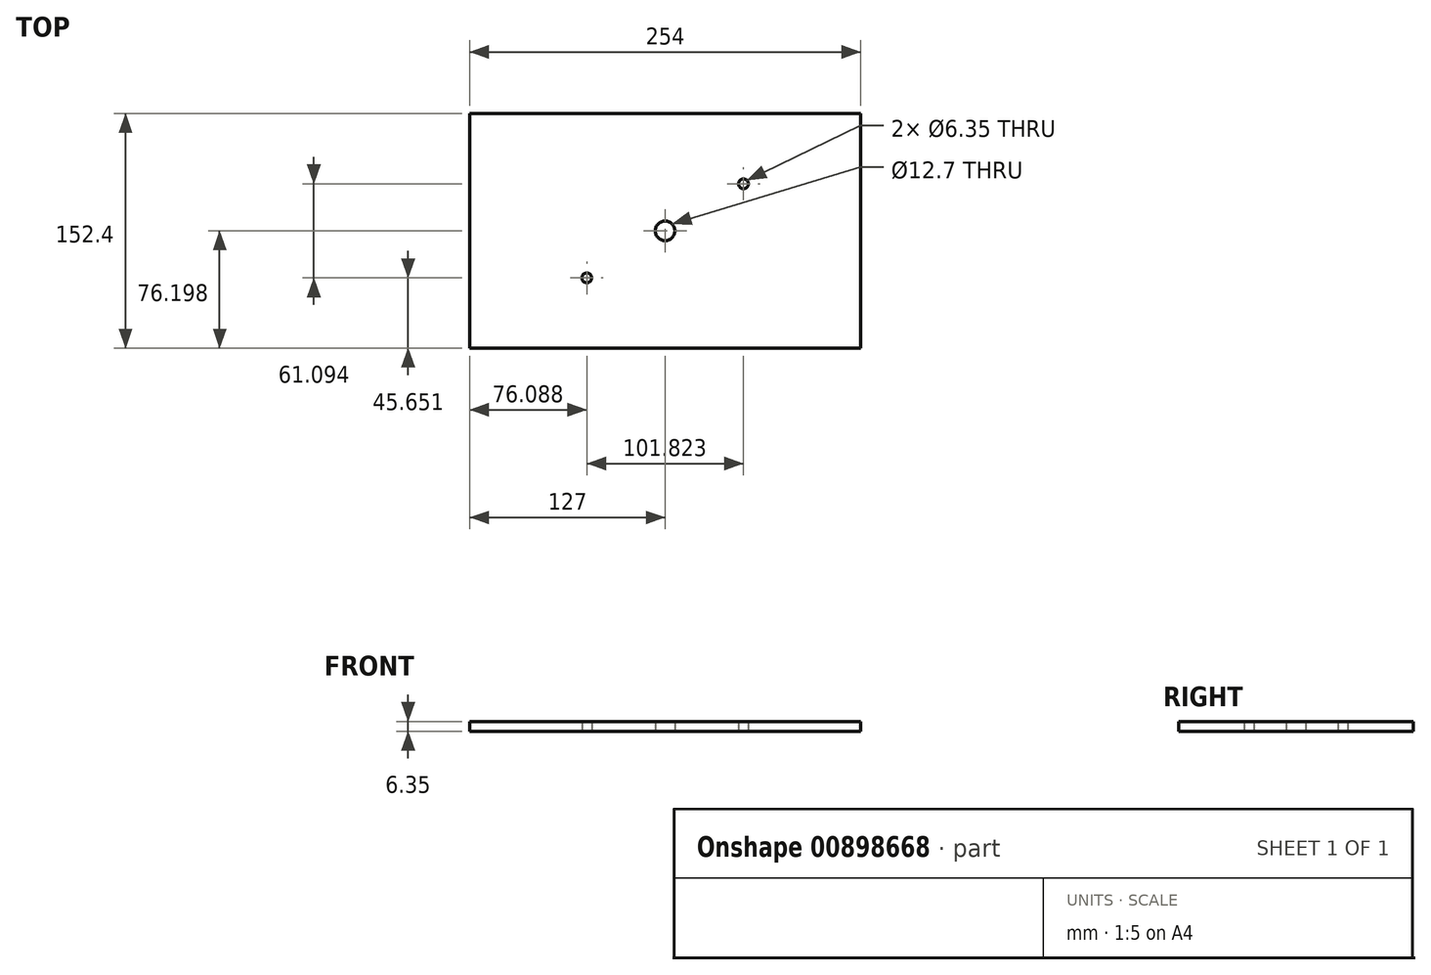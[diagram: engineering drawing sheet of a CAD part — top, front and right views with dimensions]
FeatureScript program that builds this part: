
annotation { "Feature Type Name" : "Feature", "Feature Type Description" : "" }
export const myFeature = defineFeature(function(context is Context, id is Id, definition is map)
    precondition{}
    {
        {
            var Q0;
            Q0=qCreatedBy(makeId("Top.planeOp"),FACE);
            var sketch = newSketch(context, id + "F0", { "sketchPlane" : qUnion([Q0])});
            skLineSegment(sketch, "E0", {"start": v(-26.31, -26.64) * mm, "end": v(227.69, -26.64) * mm});
            skLineSegment(sketch, "E1", {"start": v(227.69, -26.64) * mm, "end": v(227.69, 125.76) * mm});
            skLineSegment(sketch, "E2", {"start": v(227.69, 125.76) * mm, "end": v(-26.31, 125.76) * mm});
            skLineSegment(sketch, "E3", {"start": v(-26.31, 125.76) * mm, "end": v(-26.31, -26.64) * mm});
            skLineSegment(sketch, "E4", {"start": v(100.69, 125.76) * mm, "end": v(100.69, -26.64) * mm, "construction": true});
            skCircle(sketch, "E5", {"center": v(100.69, 49.56) * mm, "radius": 6.35 * mm});
            skCircle(sketch, "E6", {"center": v(151.6, 80.1) * mm, "radius": 3.18 * mm});
            skCircle(sketch, "E7", {"center": v(49.78, 19.01) * mm, "radius": 3.18 * mm});
            skSolve(sketch);
        }
        {
            var Q0;
            Q0=makeQuery(id+"F0.imprint","IMPRINT",FACE,{"disambiguationData":[TD([[makeQuery(id+"F0.imprint","IMPRINT",EDGE,{"derivedFrom":sQuery(id+"F0.wireOp",EDGE,"E0")}),1.0]])]});
            extrude(context, id + "F1", {"entities" : qUnion([Q0]), "depth" : 6.35 * mm, "offsetDistance" : 25.4 * mm});
        }
    });
